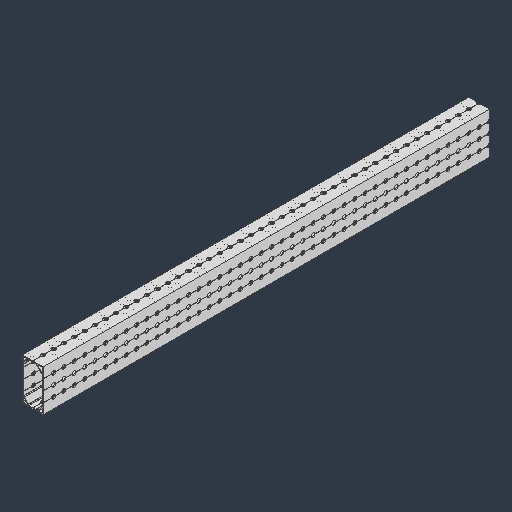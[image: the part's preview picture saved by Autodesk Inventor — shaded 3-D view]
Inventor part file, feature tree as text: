
AUTODESK INVENTOR PART (.ipt)
format: ipt  version: 2024.3 (Build 283343000, 343)  size: 3,569,664 bytes
history: native  units: mm
features: extrude x1, other x1
ambient origin geometry x8: Origin, YZ Plane, XZ Plane, XY Plane, X Axis, Y Axis, Z Axis, Center Point
bodies: Solid1 (feature_tree)
feature tree (2):
  extrude  "Extrusion1"  Depth=546.1mm
  other  "LPattern2"
